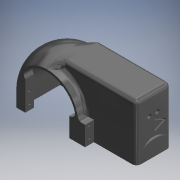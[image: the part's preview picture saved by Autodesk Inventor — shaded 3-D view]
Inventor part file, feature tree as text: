
AUTODESK INVENTOR PART (.ipt)
format: ipt  version: 2019 (Build 230136000, 136)  size: 1,101,824 bytes
history: native  units: mm (DEFAULTED — no unit token found)
features: extrude x17, sketch x15, plane x3, mirror x2, other x2, revolve x1, loft x1, fillet x1
ambient origin geometry x8: Origin, YZ Plane, XZ Plane, XY Plane, X Axis, Y Axis, Z Axis, Center Point
bodies: Solid1 (feature_tree)
feature tree (42):
  extrude  "Extrusion1"  Depth=88.9mm
  extrude  "Extrusion2"  Depth=25.4mm
  extrude  "Extrusion3"  Depth=3.175mm TaperAngle=0.0deg
  plane  "Work Plane1"
  mirror  "Mirror1"
  plane  "Work Plane2"
  revolve  "Revolution1"  [1 undecoded]
  extrude  "Extrusion5"  Depth=44.45mm
  extrude  "Extrusion8"  TaperAngle=90.0deg  [1 undecoded]
  extrude  "Extrusion10"  Depth=38.1mm
  extrude  "Extrusion11"  Depth=71.628mm
  extrude  "Extrusion12"  Depth=16.51mm TaperAngle=0.0deg
  extrude  "Extrusion13"  Depth=3.048mm
  extrude  "Extrusion14"  Depth=6.35mm
  extrude  "Extrusion16"  Depth=8.001mm
  extrude  "Extrusion17"  Depth=25.4mm TaperAngle=0.0deg
  plane  "Work Plane6"
  extrude  "Extrusion21"  Depth=3.175mm
  extrude  "Extrusion23"  Depth=6.35mm
  extrude  "Extrusion24"  Depth=68.58mm TaperAngle=0.0deg
  loft  "Loft4"
  fillet  "Fillet4"  Radius=6.35mm
  mirror  "Mirror4"
  extrude  "Extrusion25"  Depth=6.35mm
  extrude  "Extrusion26"  Depth=50.00625mm TaperAngle=0.0deg
  sketch  "Sketch1"  dims[d0=82.55mm d1=88.9mm]
  sketch  "Sketch2"  dims[d2=25.4mm d3=25.4mm]
  sketch  "Sketch3"  dims[d4=59.69mm d5=0.0mm d6=3.175mm d7=0.0mm]
  sketch  "Sketch5"  dims[d8=12.7mm d9=25.4mm]
  sketch  "Sketch8"  dims[d10=9.525mm d11=0.0mm d12=44.45mm]
  sketch  "Sketch10"  dims[d13=44.45mm d14=90.0deg]
  sketch  "Sketch15"  dims[d23=2.54mm d24=0.0mm d33=38.1mm]
  sketch  "Sketch16"  dims[d34=1.27mm d35=0.0mm d46=71.628mm]
  sketch  "Sketch21"  dims[d47=25.4mm d48=0.0mm d53=16.51mm d54=0.0mm]
  sketch  "Sketch22"  dims[d55=25.4mm d56=0.0mm d57=3.048mm]
  sketch  "Sketch26"  dims[d58=3.048mm d59=6.35mm]
  sketch  "Sketch28"  dims[d60=6.35mm d61=8.001mm]
  sketch  "Sketch29"  dims[d63=24.003mm d64=25.4mm d65=0.0mm]
  other  "Edges6"
  other  "Edges7"
  sketch  "Sketch30"  dims[d72=55.88mm d73=0.0mm d84=3.175mm]
  sketch  "Sketch31"  dims[d85=6.35mm d88=6.35mm d89=68.58mm d90=0.0mm d92=74.93mm d93=0.0mm d100=6.35mm d101=6.35mm d104=50.00625mm d105=0.0mm d109=10.16mm d110=5.08mm d111=0.0mm d112=5.08mm d113=0.0mm d114=0.0mm d115=90.0deg d116=0.0mm d117=90.0deg d118=6.35mm d119=3.175mm d120=0.0mm d121=12.7mm d122=12.7mm d123=63.5mm d124=1.5875mm d125=0.0mm]
note: 2 required parameter values undecoded (feature->parameter linkage not recoverable at this tier; creation-order binding heuristic only, values carry confidence <= 0.55)